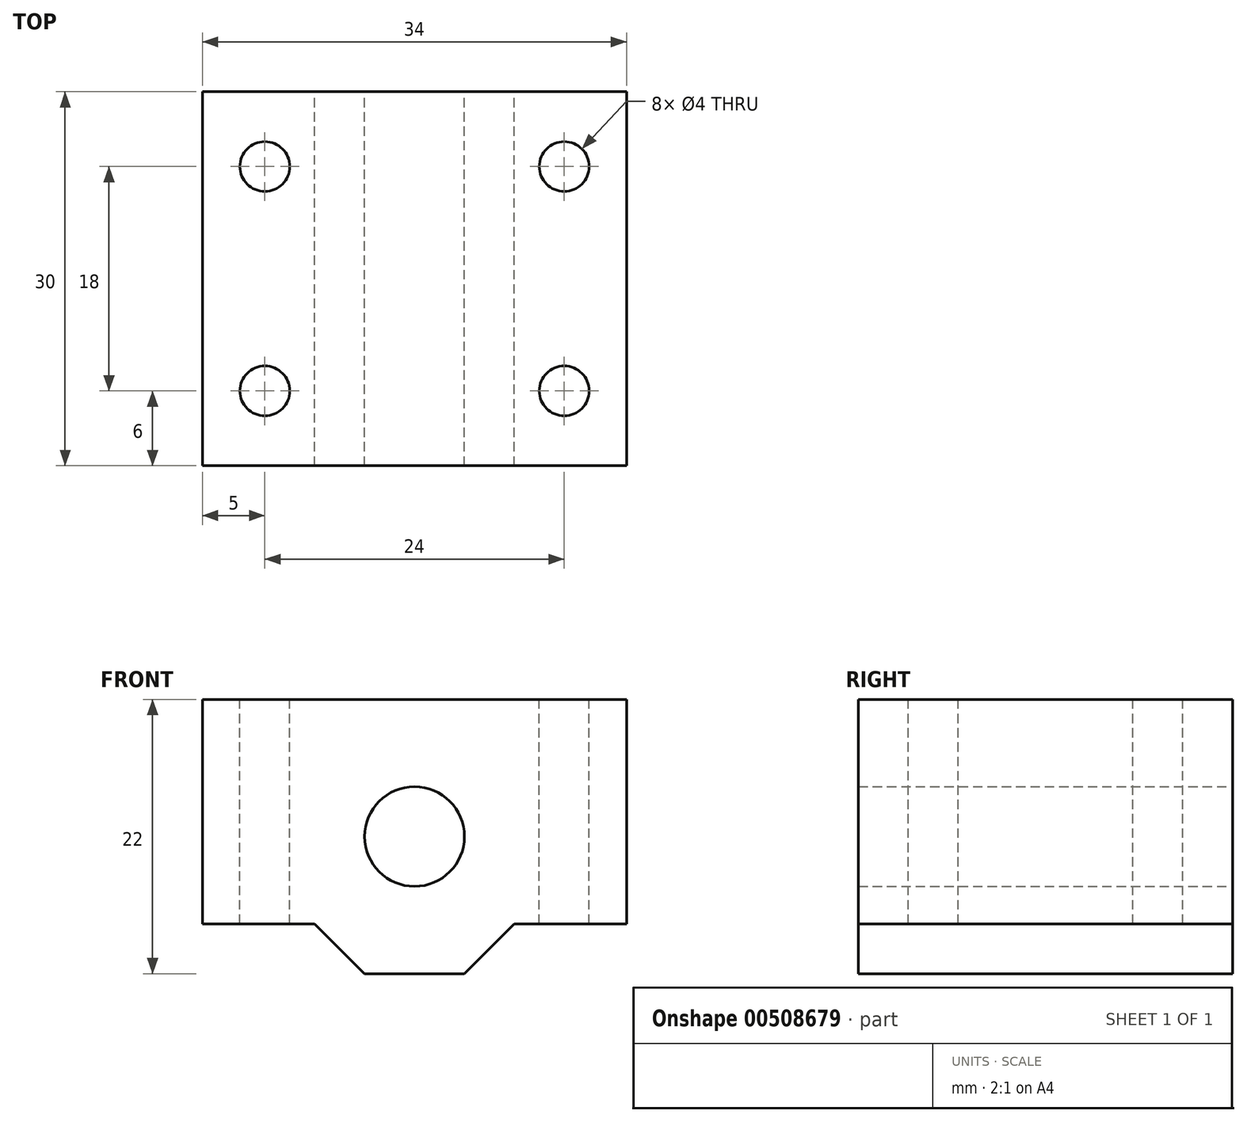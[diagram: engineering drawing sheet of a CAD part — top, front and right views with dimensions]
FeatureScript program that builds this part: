
annotation { "Feature Type Name" : "Feature", "Feature Type Description" : "" }
export const myFeature = defineFeature(function(context is Context, id is Id, definition is map)
    precondition{}
    {
        {
            var Q0;
            Q0=qCreatedBy(makeId("Front.planeOp"),FACE);
            var sketch = newSketch(context, id + "F0", { "sketchPlane" : qUnion([Q0])});
            skLineSegment(sketch, "E0", {"start": v(-17, 0) * mm, "end": v(17, 0) * mm});
            skLineSegment(sketch, "E1", {"start": v(-17, 0) * mm, "end": v(-17, -18) * mm});
            skLineSegment(sketch, "E2", {"start": v(-17, -18) * mm, "end": v(-8, -18) * mm});
            skLineSegment(sketch, "E3", {"start": v(8, -18) * mm, "end": v(17, -18) * mm});
            skLineSegment(sketch, "E4", {"start": v(17, -18) * mm, "end": v(17, 0) * mm});
            skLineSegment(sketch, "E5", {"start": v(-8, -18) * mm, "end": v(-4, -22) * mm});
            skLineSegment(sketch, "E6", {"start": v(-4, -22) * mm, "end": v(4, -22) * mm});
            skLineSegment(sketch, "E7", {"start": v(4, -22) * mm, "end": v(8, -18) * mm});
            skSolve(sketch);
        }
        {
            var Q0;
            Q0 = qSketchRegion(id + "F0", true);
            extrude(context, id + "F1", {"entities" : qUnion([Q0]), "depth" : 30 * mm, "offsetDistance" : 25 * mm});
        }
        {
            var Q0;
            Q0=makeQuery(id+"F1.opExtrude","CAP_FACE",FACE,{"disambiguationData":[OSD([sQuery(id+"F0.wireOp",EDGE,"E0"),sQuery(id+"F0.wireOp",EDGE,"E1"),sQuery(id+"F0.wireOp",EDGE,"E2"),sQuery(id+"F0.wireOp",EDGE,"E3"),sQuery(id+"F0.wireOp",EDGE,"E4"),sQuery(id+"F0.wireOp",EDGE,"E5"),sQuery(id+"F0.wireOp",EDGE,"E6"),sQuery(id+"F0.wireOp",EDGE,"E7")])],"isStart":true});
            var sketch = newSketch(context, id + "F2", { "sketchPlane" : qUnion([Q0])});
            skPoint(sketch, "E8", {"position": v(0, -11) * mm});
            skSolve(sketch);
        }
        {
            var Q0;
            Q0=sQuery(id+"F2.wireOp",VERTEX,"E8");
            var Q1;
            Q1=makeQuery(id+"F1.opExtrude","SWEPT_BODY",BODY,{"disambiguationData":[OSD([sQuery(id+"F0.wireOp",EDGE,"E0"),sQuery(id+"F0.wireOp",EDGE,"E1"),sQuery(id+"F0.wireOp",EDGE,"E2"),sQuery(id+"F0.wireOp",EDGE,"E3"),sQuery(id+"F0.wireOp",EDGE,"E4"),sQuery(id+"F0.wireOp",EDGE,"E5"),sQuery(id+"F0.wireOp",EDGE,"E6"),sQuery(id+"F0.wireOp",EDGE,"E7")])]});
            hole(context, id + "F3", {"style" : HoleStyle.SIMPLE, "endStyle" : HoleEndStyle.THROUGH, "holeDiameter" : 8 * mm, "isTappedThrough" : true, "tappedDepth" : 12 * mm, "tapClearance" : 3, "startFromSketch" : true, "locations" : qUnion([Q0]), "scope" : qUnion([Q1])});
        }
        {
            var Q0;
            Q0=makeQuery(id+"F1.opExtrude","SWEPT_FACE",FACE,{"disambiguationData":[OSD([sQuery(id+"F0.wireOp",EDGE,"E0")])]});
            var sketch = newSketch(context, id + "F4", { "sketchPlane" : qUnion([Q0])});
            skPoint(sketch, "E9", {"position": v(12, -6) * mm});
            skPoint(sketch, "E10", {"position": v(12, -24) * mm});
            skPoint(sketch, "E11", {"position": v(-12, -24) * mm});
            skPoint(sketch, "E12", {"position": v(-12, -6) * mm});
            skSolve(sketch);
        }
        {
            var Q0;
            Q0=sQuery(id+"F4.wireOp",VERTEX,"E10");
            var Q1;
            Q1=sQuery(id+"F4.wireOp",VERTEX,"E9");
            var Q2;
            Q2=sQuery(id+"F4.wireOp",VERTEX,"E12");
            var Q3;
            Q3=sQuery(id+"F4.wireOp",VERTEX,"E11");
            var Q4;
            Q4=makeQuery(id+"F1.opExtrude","SWEPT_BODY",BODY,{"disambiguationData":[OSD([sQuery(id+"F0.wireOp",EDGE,"E0"),sQuery(id+"F0.wireOp",EDGE,"E1"),sQuery(id+"F0.wireOp",EDGE,"E2"),sQuery(id+"F0.wireOp",EDGE,"E3"),sQuery(id+"F0.wireOp",EDGE,"E4"),sQuery(id+"F0.wireOp",EDGE,"E5"),sQuery(id+"F0.wireOp",EDGE,"E6"),sQuery(id+"F0.wireOp",EDGE,"E7")])]});
            hole(context, id + "F5", {"style" : HoleStyle.SIMPLE, "endStyle" : HoleEndStyle.THROUGH, "holeDiameter" : 4 * mm, "isTappedThrough" : true, "tappedDepth" : 12 * mm, "tapClearance" : 3, "startFromSketch" : true, "locations" : qUnion([Q0, Q1, Q2, Q3]), "scope" : qUnion([Q4])});
        }
    });
